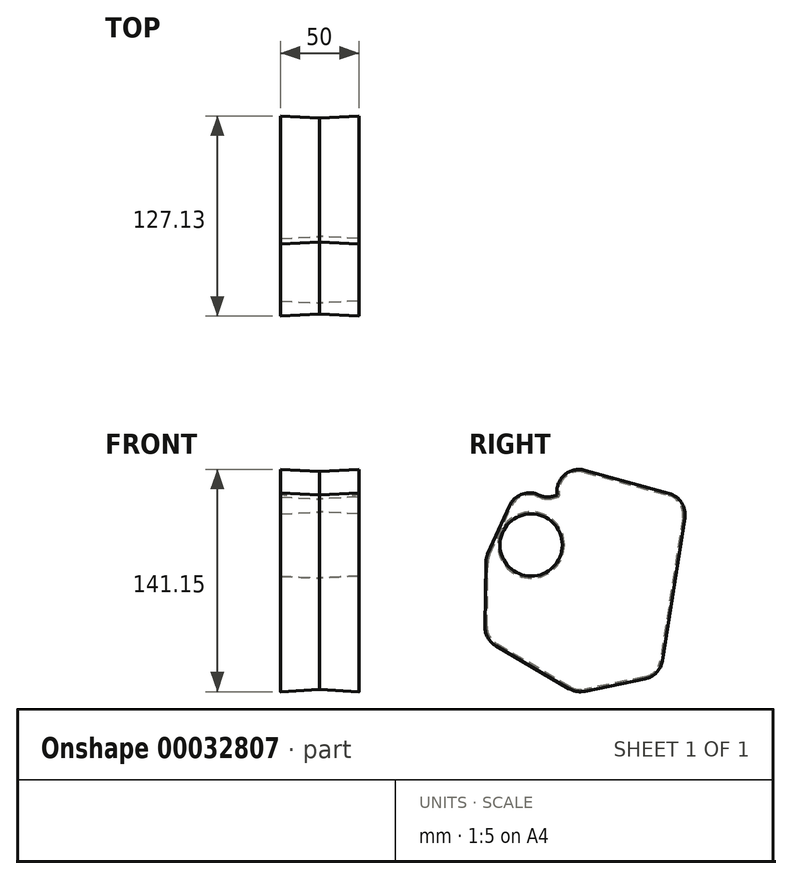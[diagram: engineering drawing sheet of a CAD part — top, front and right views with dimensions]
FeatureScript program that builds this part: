
annotation { "Feature Type Name" : "Feature", "Feature Type Description" : "" }
export const myFeature = defineFeature(function(context is Context, id is Id, definition is map)
    precondition{}
    {
        {
            var Q0;
            Q0=qCreatedBy(makeId("Right.planeOp"),FACE);
            var sketch = newSketch(context, id + "F0", { "sketchPlane" : qUnion([Q0])});
            skLineSegment(sketch, "E0", {"start": v(8.2, 84.07) * mm, "end": v(61.6, 69.42) * mm});
            skLineSegment(sketch, "E1", {"start": v(70.78, 55.2) * mm, "end": v(56.46, -35.5) * mm});
            skLineSegment(sketch, "E2", {"start": v(46.46, -45.95) * mm, "end": v(8.2, -53.76) * mm});
            skLineSegment(sketch, "E3", {"start": v(-0.74, -52.28) * mm, "end": v(-47.27, -25.07) * mm});
            skLineSegment(sketch, "E4", {"start": v(-53.56, -13.95) * mm, "end": v(-53.06, 26.5) * mm});
            skLineSegment(sketch, "E5", {"start": v(-51.95, 31.53) * mm, "end": v(-38.24, 62.19) * mm});
            skLineSegment(sketch, "E6", {"start": v(-21.96, 68.8) * mm, "end": v(-19.7, 67.9) * mm});
            skArc(sketch, "E7.filletArc", {"start": v(-21.96, 68.8) * mm, "mid": v(-31.43, 68.77) * mm, "end": v(-38.24, 62.19) * mm});
            skPoint(sketch, "E8.visualSharp", {"position": v(0.12, 39.4) * mm});
            skArc(sketch, "E8.filletArc", {"start": v(-3.9, 54.9) * mm, "mid": v(-3.9, 54.9) * mm, "end": v(-3.9, 54.9) * mm});
            skArc(sketch, "E9.filletArc", {"start": v(8.2, 84.07) * mm, "mid": v(-3.71, 81.2) * mm, "end": v(-7.66, 69.6) * mm});
            skPoint(sketch, "E10.visualSharp", {"position": v(72.56, 66.41) * mm});
            skArc(sketch, "E10.filletArc", {"start": v(70.78, 55.2) * mm, "mid": v(68.91, 64.06) * mm, "end": v(61.6, 69.42) * mm});
            skPoint(sketch, "E11.visualSharp", {"position": v(-53.66, -21.34) * mm});
            skArc(sketch, "E11.filletArc", {"start": v(-53.56, -13.95) * mm, "mid": v(-51.92, -20.36) * mm, "end": v(-47.27, -25.07) * mm});
            skPoint(sketch, "E12.visualSharp", {"position": v(-53.03, 29.13) * mm});
            skArc(sketch, "E12.filletArc", {"start": v(-51.95, 31.53) * mm, "mid": v(-52.76, 29.07) * mm, "end": v(-53.06, 26.5) * mm});
            skPoint(sketch, "E13.visualSharp", {"position": v(3.45, -54.73) * mm});
            skArc(sketch, "E13.filletArc", {"start": v(-0.74, -52.28) * mm, "mid": v(3.6, -53.84) * mm, "end": v(8.2, -53.76) * mm});
            skPoint(sketch, "E14.visualSharp", {"position": v(55.09, -44.2) * mm});
            skArc(sketch, "E14.filletArc", {"start": v(46.46, -45.95) * mm, "mid": v(53.1, -42.29) * mm, "end": v(56.46, -35.5) * mm});
            skLineSegment(sketch, "E15", {"start": v(-11.61, 67.48) * mm, "end": v(-8.43, 68.36) * mm});
            skPoint(sketch, "E16.visualSharp", {"position": v(-15.73, 66.33) * mm});
            skArc(sketch, "E16.filletArc", {"start": v(-19.7, 67.9) * mm, "mid": v(-15.7, 67.03) * mm, "end": v(-11.61, 67.48) * mm});
            skPoint(sketch, "E17.visualSharp", {"position": v(-7.45, 68.64) * mm});
            skArc(sketch, "E17.filletArc", {"start": v(-8.43, 68.36) * mm, "mid": v(-7.8, 68.83) * mm, "end": v(-7.66, 69.6) * mm});
            skCircle(sketch, "E18", {"center": v(-32.9, 45.1) * mm, "radius": 9.48 * mm});
            skCircle(sketch, "E19", {"center": v(-25.53, 37.84) * mm, "radius": 21.08 * mm});
            skSolve(sketch);
        }
        {
            var Q0;
            Q0 = qSketchRegion(id + "F0", true);
            extrude(context, id + "F1", {"entities" : qUnion([Q0]), "depth" : 25 * mm, "hasDraft" : true, "draftAngle" : 3 * degree, "hasSecondDirection" : true, "secondDirectionOppositeDirection" : true, "secondDirectionDepth" : 25 * mm, "hasSecondDirectionDraft" : true, "secondDirectionDraftAngle" : 3 * degree});
        }
    });
